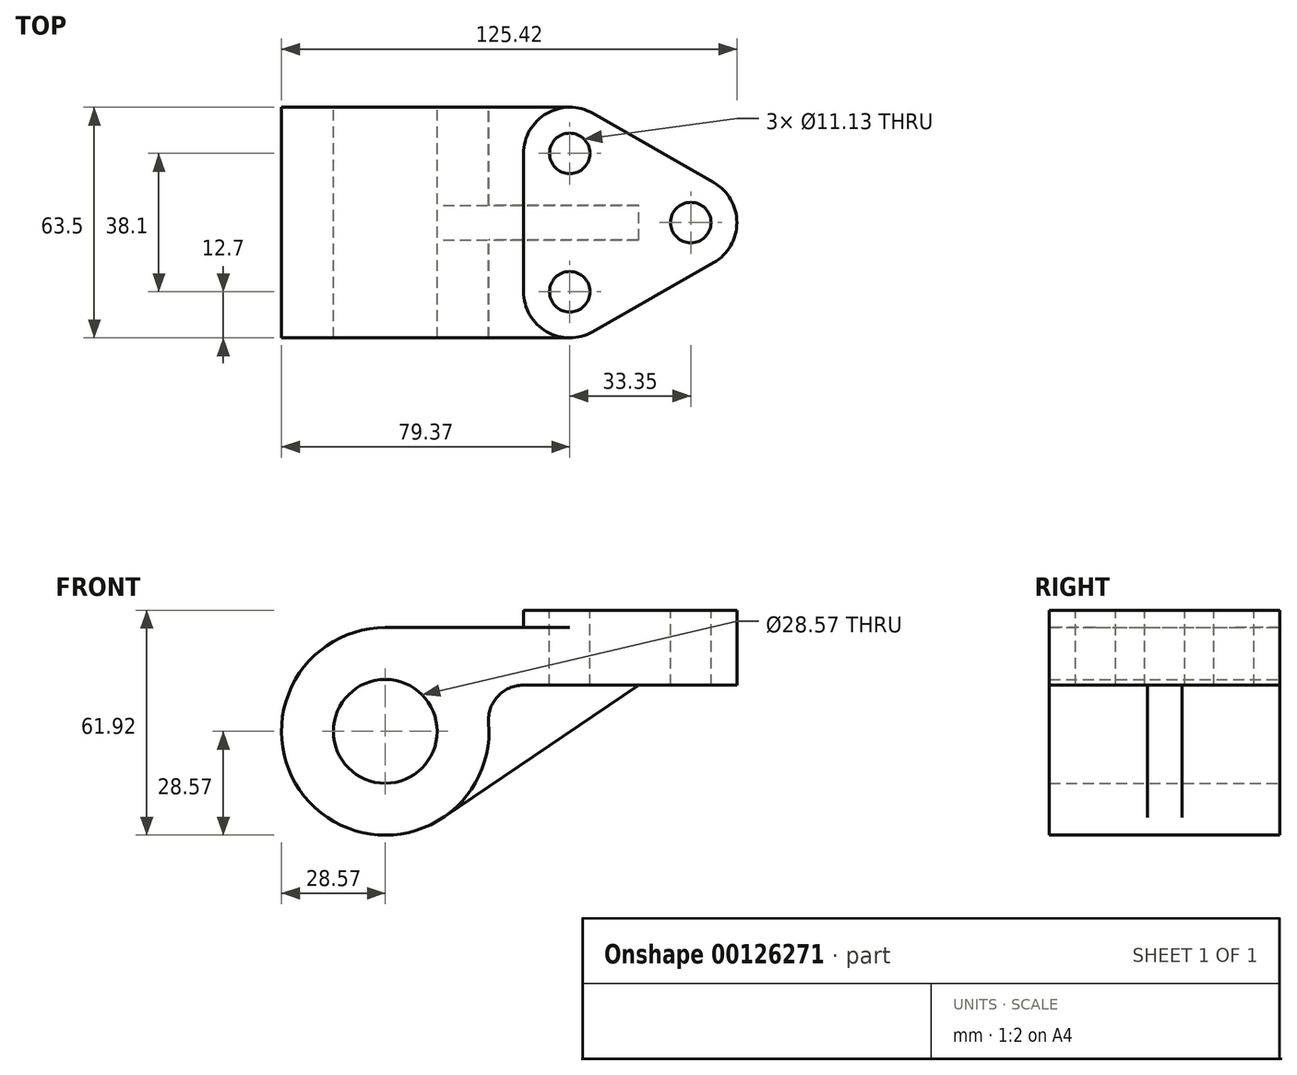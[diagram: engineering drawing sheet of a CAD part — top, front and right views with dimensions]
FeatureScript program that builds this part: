
annotation { "Feature Type Name" : "Feature", "Feature Type Description" : "" }
export const myFeature = defineFeature(function(context is Context, id is Id, definition is map)
    precondition{}
    {
        {
            var Q0;
            Q0=qCreatedBy(makeId("Front.planeOp"),FACE);
            var sketch = newSketch(context, id + "F0", { "sketchPlane" : qUnion([Q0])});
            skCircle(sketch, "E0", {"center": v(0, 0) * mm, "radius": 14.29 * mm});
            skArc(sketch, "E1", {"start": v(0, 28.58) * mm, "mid": v(-19.35, -21.03) * mm, "end": v(28.48, 2.38) * mm});
            skLineSegment(sketch, "E2", {"start": v(0, 28.58) * mm, "end": v(38.1, 28.58) * mm});
            skLineSegment(sketch, "E3", {"start": v(38.1, 28.58) * mm, "end": v(38.1, 33.35) * mm});
            skLineSegment(sketch, "E4", {"start": v(38.1, 33.35) * mm, "end": v(96.85, 33.35) * mm});
            skLineSegment(sketch, "E5", {"start": v(96.85, 33.35) * mm, "end": v(96.85, 12.7) * mm});
            skLineSegment(sketch, "E6", {"start": v(96.85, 12.7) * mm, "end": v(37.97, 12.7) * mm});
            skLineSegment(sketch, "E7", {"start": v(16, -23.68) * mm, "end": v(69.85, 12.7) * mm});
            skPoint(sketch, "E8.visualSharp", {"position": v(25.6, 12.7) * mm});
            skArc(sketch, "E8.filletArc", {"start": v(37.97, 12.7) * mm, "mid": v(30.96, 9.62) * mm, "end": v(28.48, 2.38) * mm});
            skSolve(sketch);
        }
        {
            var Q0;
            Q0=makeQuery(id+"F0.imprint","IMPRINT",FACE,{"disambiguationData":[TD([[makeQuery(id+"F0.imprint","IMPRINT",EDGE,{"derivedFrom":sQuery(id+"F0.wireOp",EDGE,"E0")}),-1.0]])]});
            extrude(context, id + "F1", {"entities" : qUnion([Q0]), "endBound" : BoundingType.SYMMETRIC, "depth" : 63.5 * mm});
        }
        {
            var Q0;
            {var subQ2=sQuery(id+"F0.wireOp",EDGE,"E7");Q0=makeQuery(id+"F0.imprint","IMPRINT",FACE,{"disambiguationData":[TD([[makeQuery(id+"F0.imprint","IMPRINT",EDGE,{"derivedFrom":subQ2}),1.0]])]});}
            extrude(context, id + "F2", {"entities" : qUnion([Q0]), "operationType" : NewBodyOperationType.ADD, "endBound" : BoundingType.SYMMETRIC, "depth" : 9.52 * mm});
        }
        {
            var Q0;
            Q0=makeQuery(id+"F1.opExtrude","SWEPT_FACE",FACE,{"disambiguationData":[OSD([sQuery(id+"F0.wireOp",EDGE,"E4")])]});
            var sketch = newSketch(context, id + "F3", { "sketchPlane" : qUnion([Q0])});
            skCircle(sketch, "E9", {"center": v(84.15, 0) * mm, "radius": 5.56 * mm});
            skCircle(sketch, "E10", {"center": v(50.8, 19.05) * mm, "radius": 5.56 * mm});
            skCircle(sketch, "E11", {"center": v(50.8, -19.05) * mm, "radius": 5.56 * mm});
            skArc(sketch, "E12", {"start": v(57.1, 30.08) * mm, "mid": v(44.42, 30.03) * mm, "end": v(38.1, 19.05) * mm});
            skArc(sketch, "E13", {"start": v(90.45, -11.03) * mm, "mid": v(96.85, 0) * mm, "end": v(90.45, 11.03) * mm});
            skLineSegment(sketch, "E14", {"start": v(57.1, 30.08) * mm, "end": v(90.45, 11.03) * mm});
            skLineSegment(sketch, "E15", {"start": v(90.45, -11.03) * mm, "end": v(57.1, -30.08) * mm});
            skLineSegment(sketch, "E16", {"start": v(38.1, 19.05) * mm, "end": v(38.1, -19.05) * mm});
            skArc(sketch, "E17", {"start": v(57.1, -30.08) * mm, "mid": v(44.42, -30.03) * mm, "end": v(38.1, -19.05) * mm});
            skLineSegment(sketch, "E18", {"start": v(38.1, 19.05) * mm, "end": v(38.1, 31.75) * mm});
            skLineSegment(sketch, "E19", {"start": v(96.85, 31.75) * mm, "end": v(96.85, 0) * mm});
            skLineSegment(sketch, "E20", {"start": v(96.85, 0) * mm, "end": v(96.85, -31.75) * mm});
            skLineSegment(sketch, "E21", {"start": v(96.85, -31.75) * mm, "end": v(96.85, 0) * mm});
            skSolve(sketch);
        }
        {
            var Q0;
            {var subQ0=sQuery(id+"F3.wireOp",EDGE,"E14");Q0=makeQuery(id+"F3.imprint","IMPRINT",FACE,{"disambiguationData":[TD([[makeQuery(id+"F3.imprint","IMPRINT",EDGE,{"derivedFrom":subQ0}),1.0]])]});}
            extrude(context, id + "F4", {"entities" : qUnion([Q0]), "operationType" : NewBodyOperationType.REMOVE, "oppositeDirection" : true, "depth" : 25.4 * mm});
        }
        {
            var Q0;
            {var subQ2=sQuery(id+"F3.wireOp",EDGE,"E15");Q0=makeQuery(id+"F3.imprint","IMPRINT",FACE,{"disambiguationData":[TD([[makeQuery(id+"F3.imprint","IMPRINT",EDGE,{"derivedFrom":subQ2}),1.0]])]});}
            extrude(context, id + "F5", {"entities" : qUnion([Q0]), "operationType" : NewBodyOperationType.REMOVE, "oppositeDirection" : true, "depth" : 25.4 * mm});
        }
        {
            var Q0;
            {var subQ0=sQuery(id+"F3.wireOp",EDGE,"E17");var subQ1=sQuery(id+"F0.wireOp",EDGE,"E4");var subQ4=makeQuery(id+"F1.opExtrude","CAP_EDGE",EDGE,{"disambiguationData":[OSD([subQ1])],"isStart":false});var subQ5=makeQuery(id+"F3.imprint","INTERSECT",VERTEX,{"derivedFrom":[subQ4,subQ0]});Q0=makeQuery(id+"F3.imprint","IMPRINT",FACE,{"disambiguationData":[TD([[makeQuery(id+"F3.imprint","IMPRINT",EDGE,{"disambiguationData":[TD([[subQ5,1.0]])],"derivedFrom":subQ4}),1.0]])]});}
            var Q1;
            {var subQ0=sQuery(id+"F3.wireOp",EDGE,"E18");Q1=makeQuery(id+"F3.imprint","IMPRINT",FACE,{"disambiguationData":[TD([[makeQuery(id+"F3.imprint","IMPRINT",EDGE,{"derivedFrom":subQ0}),-1.0]])]});}
            extrude(context, id + "F6", {"entities" : qUnion([Q0, Q1]), "operationType" : NewBodyOperationType.REMOVE, "oppositeDirection" : true, "depth" : 4.78 * mm});
        }
        {
            var Q0;
            Q0=makeQuery(id+"F3.imprint","IMPRINT",FACE,{"disambiguationData":[TD([[makeQuery(id+"F3.imprint","IMPRINT",EDGE,{"derivedFrom":sQuery(id+"F3.wireOp",EDGE,"E9")}),1.0]])]});
            var Q1;
            Q1=makeQuery(id+"F3.imprint","IMPRINT",FACE,{"disambiguationData":[TD([[makeQuery(id+"F3.imprint","IMPRINT",EDGE,{"derivedFrom":sQuery(id+"F3.wireOp",EDGE,"E10")}),1.0]])]});
            var Q2;
            Q2=makeQuery(id+"F3.imprint","IMPRINT",FACE,{"disambiguationData":[TD([[makeQuery(id+"F3.imprint","IMPRINT",EDGE,{"derivedFrom":sQuery(id+"F3.wireOp",EDGE,"E11")}),1.0]])]});
            extrude(context, id + "F7", {"entities" : qUnion([Q0, Q1, Q2]), "operationType" : NewBodyOperationType.REMOVE, "oppositeDirection" : true, "depth" : 25.4 * mm});
        }
    });
